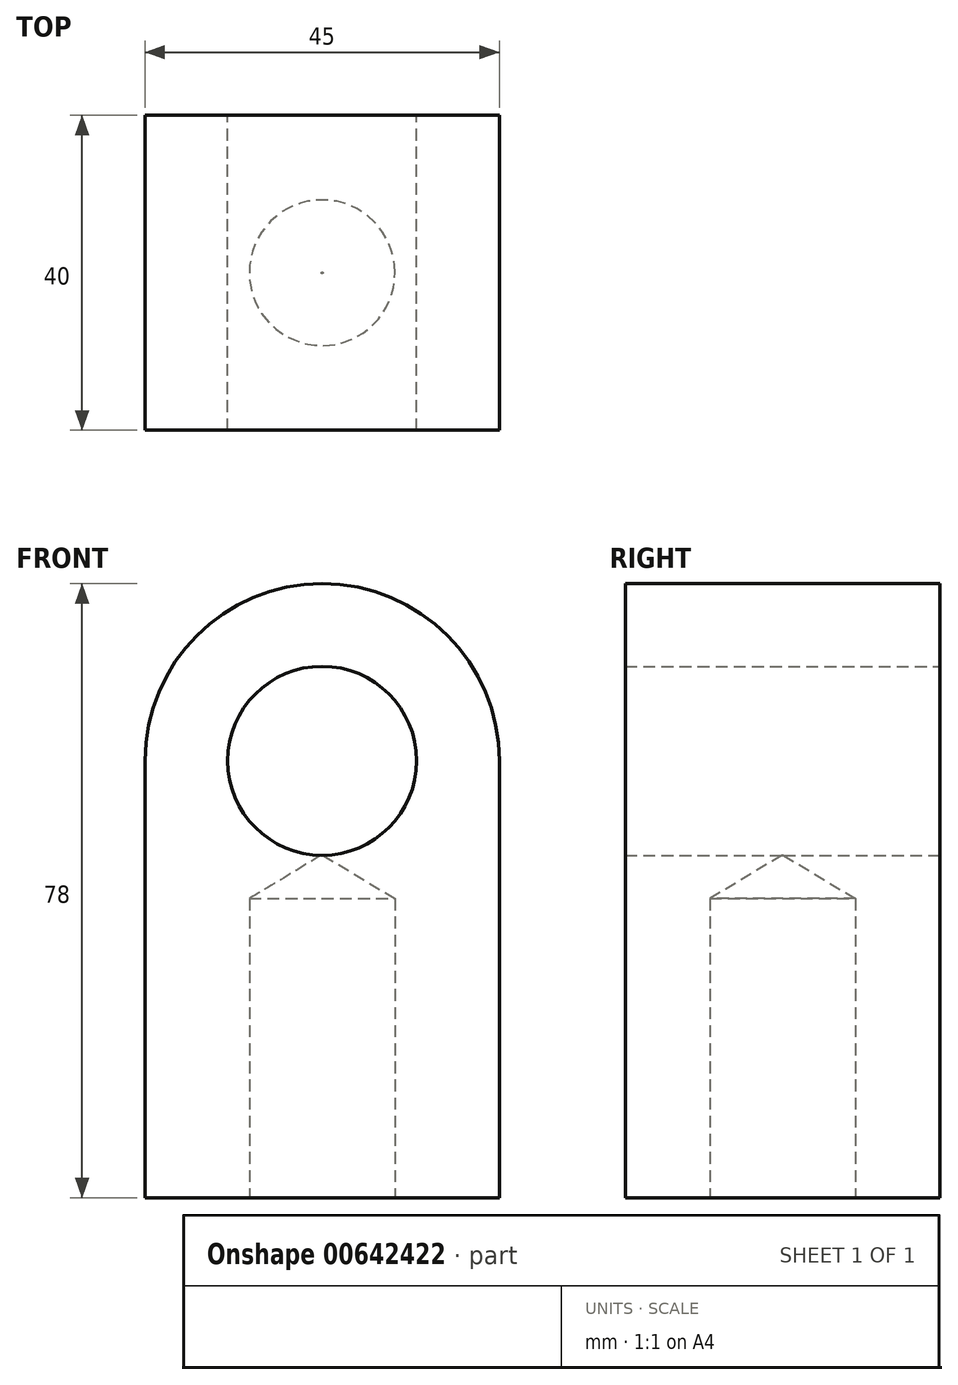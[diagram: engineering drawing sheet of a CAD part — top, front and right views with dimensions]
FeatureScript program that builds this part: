
annotation { "Feature Type Name" : "Feature", "Feature Type Description" : "" }
export const myFeature = defineFeature(function(context is Context, id is Id, definition is map)
    precondition{}
    {
        {
            var Q0;
            Q0=qCreatedBy(makeId("Front.planeOp"),FACE);
            var sketch = newSketch(context, id + "F0", { "sketchPlane" : qUnion([Q0])});
            skLineSegment(sketch, "E0.top", {"start": v(22.5, -39) * mm, "end": v(-22.5, -39) * mm});
            skLineSegment(sketch, "E0.left", {"start": v(22.5, 16.5) * mm, "end": v(22.5, -39) * mm});
            skLineSegment(sketch, "E0.right", {"start": v(-22.5, 16.5) * mm, "end": v(-22.5, -39) * mm});
            skPoint(sketch, "E0.middle", {"position": v(0, 0) * mm});
            skArc(sketch, "E1", {"start": v(22.5, 16.5) * mm, "mid": v(0, 39) * mm, "end": v(-22.5, 16.5) * mm});
            skCircle(sketch, "E2", {"center": v(0, 16.5) * mm, "radius": 12 * mm});
            skSolve(sketch);
        }
        {
            var Q0;
            Q0=makeQuery(id+"F0.imprint","IMPRINT",FACE,{"disambiguationData":[TD([[makeQuery(id+"F0.imprint","IMPRINT",EDGE,{"derivedFrom":sQuery(id+"F0.wireOp",EDGE,"E0.top")}),-1.0]])]});
            extrude(context, id + "F1", {"entities" : qUnion([Q0]), "depth" : 40 * mm, "offsetDistance" : 25 * mm});
        }
        {
            var Q0;
            Q0=makeQuery(id+"F1.opExtrude","SWEPT_FACE",FACE,{"disambiguationData":[OSD([sQuery(id+"F0.wireOp",EDGE,"E0.top")])]});
            var sketch = newSketch(context, id + "F2", { "sketchPlane" : qUnion([Q0])});
            skPoint(sketch, "E3", {"position": v(0, 20) * mm});
            skPoint(sketch, "E3.positionSnap0", {"position": v(22.5, 20) * mm});
            skPoint(sketch, "E3.positionSnap1", {"position": v(0, 40) * mm});
            skSolve(sketch);
        }
        {
            var Q0;
            Q0=sQuery(id+"F2.wireOp",VERTEX,"E3");
            var Q1;
            Q1=makeQuery(id+"F1.opExtrude","SWEPT_BODY",BODY,{"disambiguationData":[OSD([sQuery(id+"F0.wireOp",EDGE,"E0.top"),sQuery(id+"F0.wireOp",EDGE,"E0.left"),sQuery(id+"F0.wireOp",EDGE,"E0.right"),sQuery(id+"F0.wireOp",EDGE,"E1"),sQuery(id+"F0.wireOp",EDGE,"E2")])]});
            hole(context, id + "F3", {"style" : HoleStyle.SIMPLE, "endStyle" : HoleEndStyle.BLIND, "standardTappedOrClearance" : lookupTablePath({ "standard" : "ISO", "engagement" : "75%", "pitch" : "1.5 mm", "size" : "M20", "type" : "Tapped" }), "standardBlindInLast" : lookupTablePath({ "standard" : "ISO", "engagement" : "75%", "pitch" : "1.5 mm", "size" : "M20", "type" : "Tapped" }), "holeDiameter" : 18.5 * mm, "majorDiameter" : 20 * mm, "showTappedDepth" : true, "holeDepth" : 38 * mm, "tappedDepth" : 35 * mm, "tapClearance" : 2, "locations" : qUnion([Q0]), "scope" : qUnion([Q1])});
        }
    });
